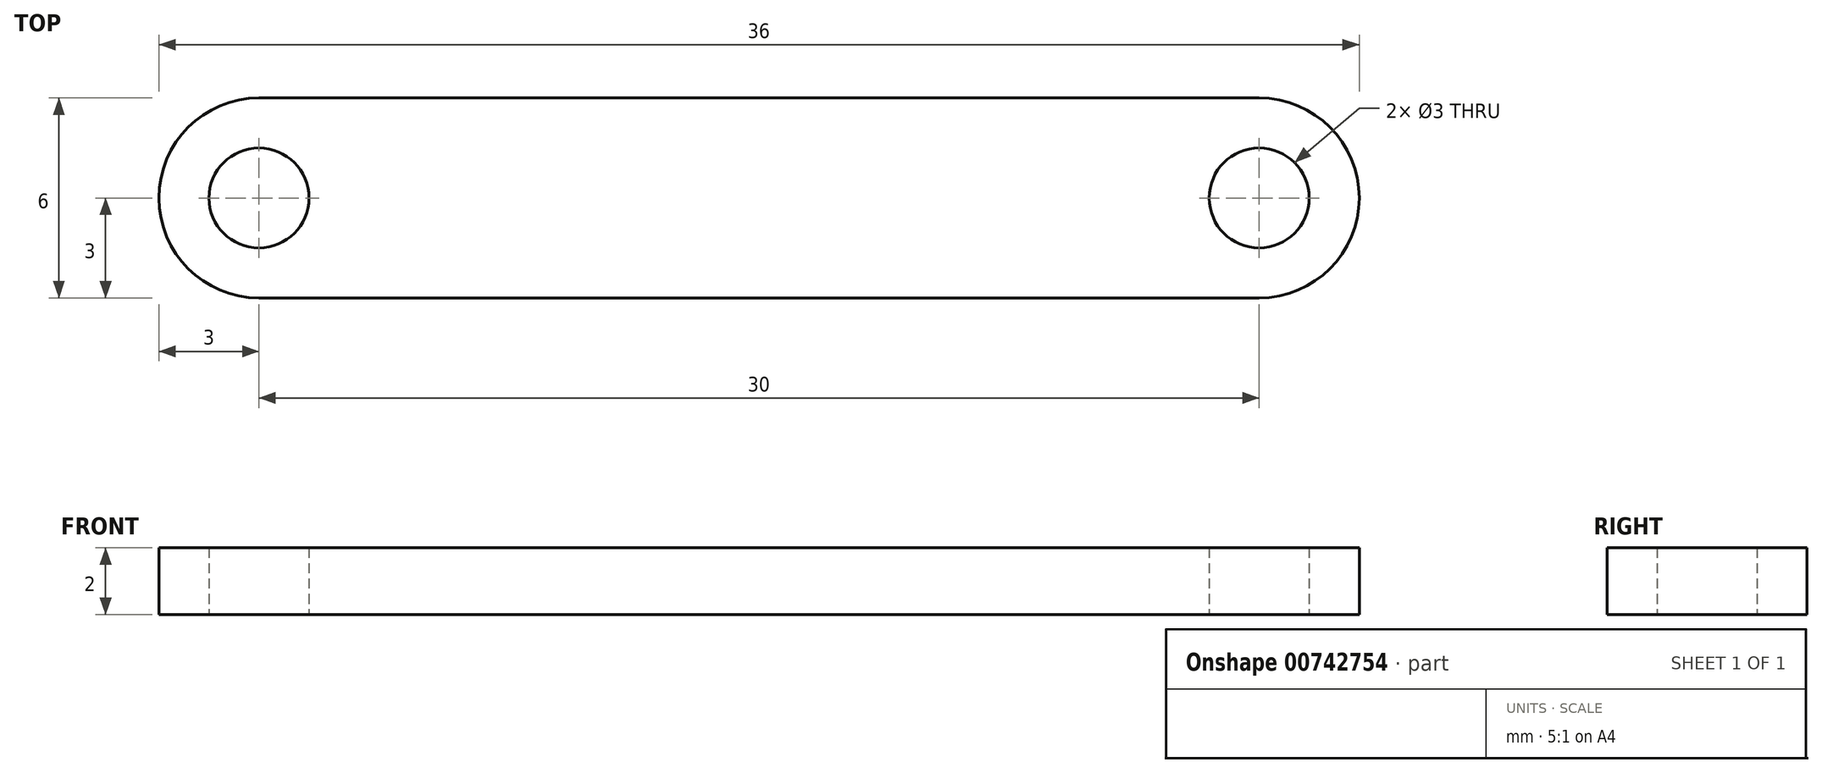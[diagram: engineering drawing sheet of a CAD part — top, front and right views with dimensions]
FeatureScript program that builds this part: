
annotation { "Feature Type Name" : "Feature", "Feature Type Description" : "" }
export const myFeature = defineFeature(function(context is Context, id is Id, definition is map)
    precondition{}
    {
        {
            var Q0;
            Q0=qCreatedBy(makeId("Top.planeOp"),FACE);
            var sketch = newSketch(context, id + "F0", { "sketchPlane" : qUnion([Q0])});
            skLineSegment(sketch, "E0.bottom", {"start": v(15, -3) * mm, "end": v(-15, -3) * mm});
            skLineSegment(sketch, "E0.top", {"start": v(15, 3) * mm, "end": v(-15, 3) * mm});
            skPoint(sketch, "E0.middle", {"position": v(0, 0) * mm});
            skArc(sketch, "E1", {"start": v(-15, 3) * mm, "mid": v(-18, 0) * mm, "end": v(-15, -3) * mm});
            skArc(sketch, "E2", {"start": v(15, -3) * mm, "mid": v(18, 0) * mm, "end": v(15, 3) * mm});
            skCircle(sketch, "E3", {"center": v(-15, 0) * mm, "radius": 1.5 * mm});
            skCircle(sketch, "E4", {"center": v(15, 0) * mm, "radius": 1.5 * mm});
            skSolve(sketch);
        }
        {
            var Q0;
            Q0 = qSketchRegion(id + "F0", true);
            extrude(context, id + "F1", {"entities" : qUnion([Q0]), "depth" : 2 * mm, "offsetDistance" : 25 * mm});
        }
    });
